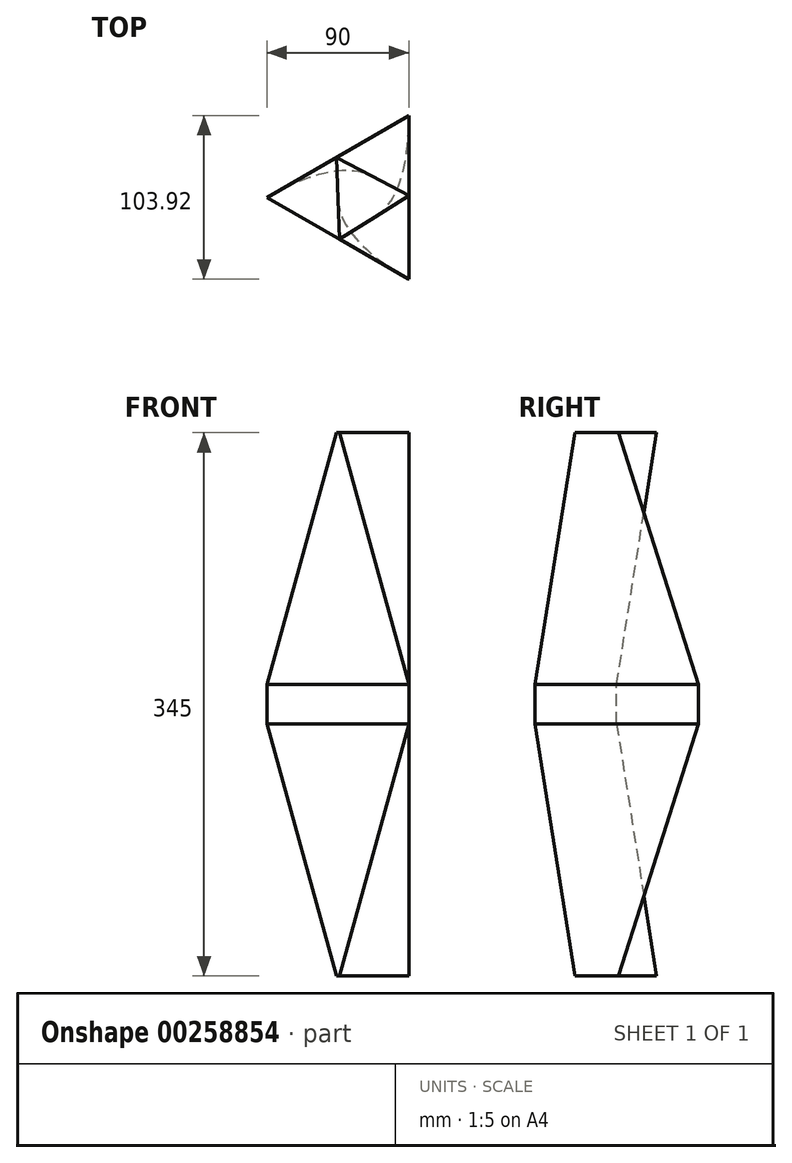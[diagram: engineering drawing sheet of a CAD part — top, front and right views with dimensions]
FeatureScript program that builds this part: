
annotation { "Feature Type Name" : "Feature", "Feature Type Description" : "" }
export const myFeature = defineFeature(function(context is Context, id is Id, definition is map)
    precondition{}
    {
        {
            var Q0;
            Q0=qCreatedBy(makeId("Top.planeOp"),FACE);
            var sketch = newSketch(context, id + "F0", { "sketchPlane" : qUnion([Q0])});
            skCircle(sketch, "E0.cCircle", {"center": v(0, 0) * mm, "radius": 60 * mm, "construction": true});
            skLineSegment(sketch, "E0.0", {"start": v(-60, 0) * mm, "end": v(30, 51.96) * mm});
            skLineSegment(sketch, "E0.1", {"start": v(30, 51.96) * mm, "end": v(30, -51.96) * mm});
            skLineSegment(sketch, "E0.2", {"start": v(30, -51.96) * mm, "end": v(-60, 0) * mm});
            skSolve(sketch);
        }
        {
            var Q0;
            Q0=qCreatedBy(makeId("Top.planeOp"),FACE);
            cPlane(context, id + "F1", {"entities" : qUnion([Q0]), "cplaneType" : CPlaneType.OFFSET, "offset" : 160 * mm, "width" : 150 * mm, "height" : 150 * mm});
        }
        {
            var Q0;
            Q0=qCreatedBy(id+"F1.planeOp",FACE);
            var sketch = newSketch(context, id + "F2", { "sketchPlane" : qUnion([Q0])});
            skCircle(sketch, "E1.cCircle", {"center": v(0, 0) * mm, "radius": 30 * mm, "construction": true});
            skLineSegment(sketch, "E1.0", {"start": v(-14, -26.53) * mm, "end": v(-15.97, 25.4) * mm});
            skLineSegment(sketch, "E1.1", {"start": v(-15.97, 25.4) * mm, "end": v(29.98, 1.13) * mm});
            skLineSegment(sketch, "E1.2", {"start": v(29.98, 1.13) * mm, "end": v(-14, -26.53) * mm});
            skSolve(sketch);
        }
        {
            var Q0;
            Q0=makeQuery(id+"F0.imprint","IMPRINT",FACE,{"disambiguationData":[TD([[makeQuery(id+"F0.imprint","IMPRINT",EDGE,{"derivedFrom":sQuery(id+"F0.wireOp",EDGE,"E0.0")}),-1.0]])]});
            var Q1;
            Q1=makeQuery(id+"F2.imprint","IMPRINT",FACE,{"disambiguationData":[TD([[makeQuery(id+"F2.imprint","IMPRINT",EDGE,{"derivedFrom":sQuery(id+"F2.wireOp",EDGE,"E1.0")}),-1.0]])]});
            loft(context, id + "F3", {"sheetProfilesArray" : [{ "sheetProfileEntities" : qUnion([Q0]) }, { "sheetProfileEntities" : qUnion([Q1]) }]});
        }
        {
            var Q0;
            Q0=makeQuery(id+"F3.opLoft","CAP_FACE",FACE,{"disambiguationData":[OSD([makeQuery(id+"F0.imprint","IMPRINT",FACE,{"disambiguationData":[TD([[makeQuery(id+"F0.imprint","IMPRINT",EDGE,{"derivedFrom":sQuery(id+"F0.wireOp",EDGE,"E0.0")}),-1.0]])]})])],"isStart":true});
            extrude(context, id + "F4", {"entities" : qUnion([Q0]), "depth" : 25 * mm});
        }
        {
            var Q0;
            Q0=makeQuery(id+"F4.opExtrude","CAP_FACE",FACE,{"disambiguationData":[OSD([makeQuery(id+"F0.imprint","IMPRINT",FACE,{"disambiguationData":[TD([[makeQuery(id+"F0.imprint","IMPRINT",EDGE,{"derivedFrom":sQuery(id+"F0.wireOp",EDGE,"E0.0")}),-1.0]])]})])],"isStart":false});
            cPlane(context, id + "F5", {"entities" : qUnion([Q0]), "cplaneType" : CPlaneType.OFFSET, "offset" : 12.5 * mm, "oppositeDirection" : true, "width" : 150 * mm, "height" : 150 * mm});
        }
        {
            var Q0;
            Q0=makeQuery(id+"F3.opLoft","SWEPT_BODY",BODY,{"disambiguationData":[OSD([makeQuery(id+"F0.imprint","IMPRINT",FACE,{"disambiguationData":[TD([[makeQuery(id+"F0.imprint","IMPRINT",EDGE,{"derivedFrom":sQuery(id+"F0.wireOp",EDGE,"E0.0")}),-1.0]])]}),makeQuery(id+"F2.imprint","IMPRINT",FACE,{"disambiguationData":[TD([[makeQuery(id+"F2.imprint","IMPRINT",EDGE,{"derivedFrom":sQuery(id+"F2.wireOp",EDGE,"E1.0")}),-1.0]])]})])]});
            var Q1;
            Q1=qCreatedBy(id+"F5.planeOp",FACE);
            mirror(context, id + "F6", {"entities" : qUnion([Q0]), "mirrorPlane" : qUnion([Q1])});
        }
    });
